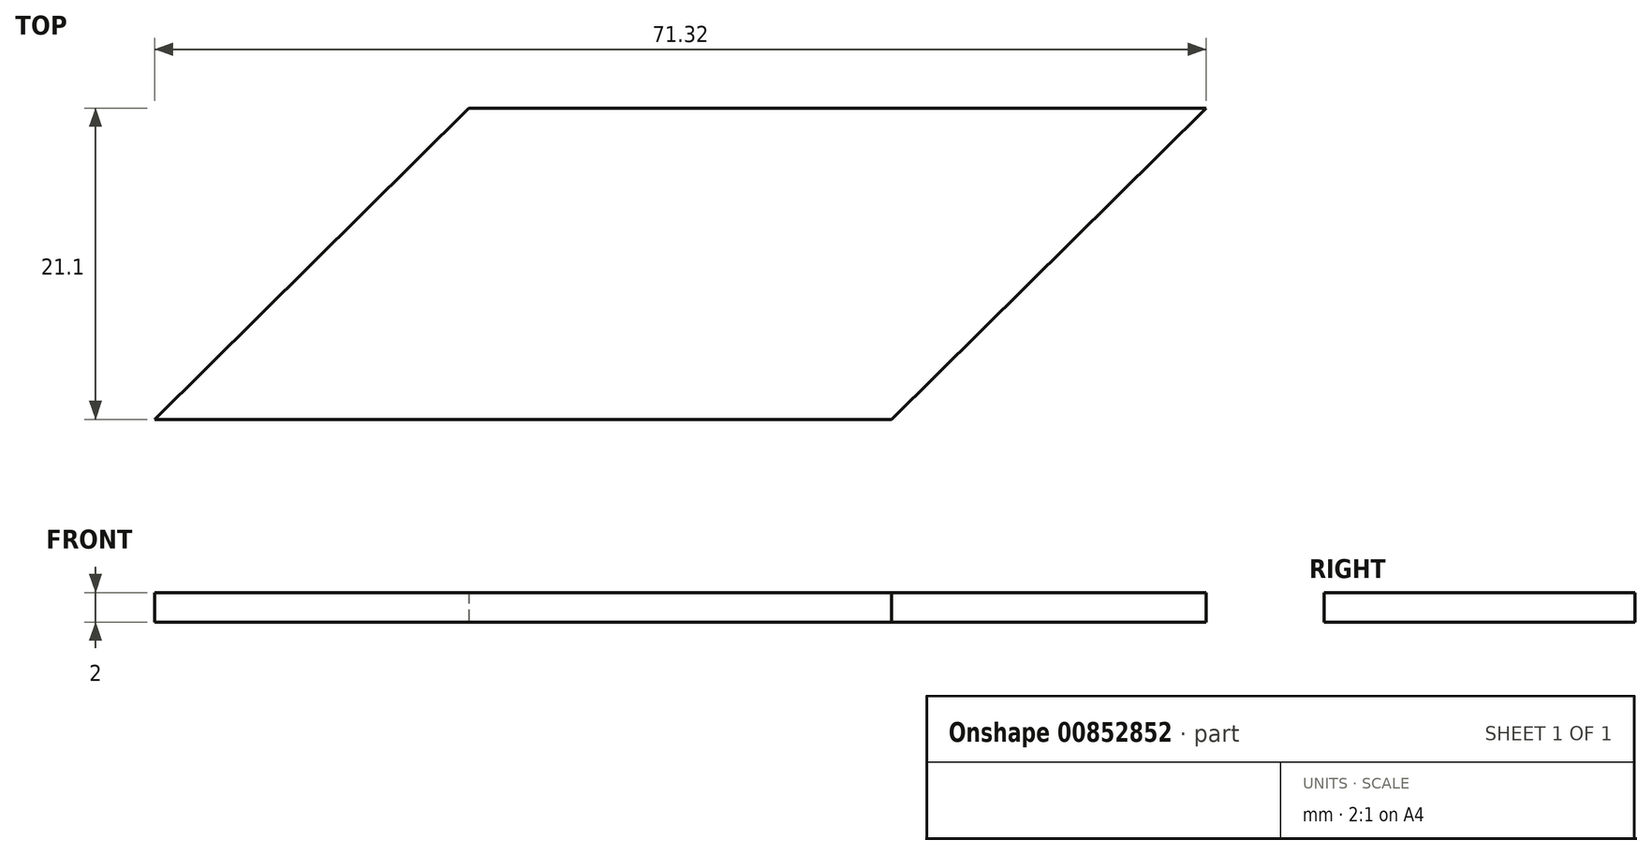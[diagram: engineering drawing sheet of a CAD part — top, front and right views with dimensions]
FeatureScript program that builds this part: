
annotation { "Feature Type Name" : "Feature", "Feature Type Description" : "" }
export const myFeature = defineFeature(function(context is Context, id is Id, definition is map)
    precondition{}
    {
        {
            var Q0;
            Q0=qCreatedBy(makeId("Top.planeOp"),FACE);
            var sketch = newSketch(context, id + "F0", { "sketchPlane" : qUnion([Q0])});
            skLineSegment(sketch, "E0", {"start": v(-50, 0) * mm, "end": v(0, 0) * mm});
            skLineSegment(sketch, "E1", {"start": v(-50, 0) * mm, "end": v(-28.68, 21.1) * mm});
            skLineSegment(sketch, "E2", {"start": v(-28.68, 21.1) * mm, "end": v(21.32, 21.1) * mm});
            skLineSegment(sketch, "E3", {"start": v(21.32, 21.1) * mm, "end": v(0, 0) * mm});
            skSolve(sketch);
        }
        {
            var Q0;
            Q0=makeQuery(id+"F0.imprint","IMPRINT",FACE,{"disambiguationData":[TD([[makeQuery(id+"F0.imprint","IMPRINT",EDGE,{"derivedFrom":sQuery(id+"F0.wireOp",EDGE,"E0")}),1.0]])]});
            extrude(context, id + "F1", {"entities" : qUnion([Q0]), "depth" : 2 * mm, "offsetDistance" : 25 * mm});
        }
    });
